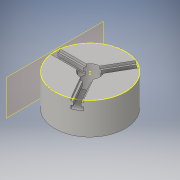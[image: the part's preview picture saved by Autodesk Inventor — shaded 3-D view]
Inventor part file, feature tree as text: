
AUTODESK INVENTOR PART (.ipt)
format: ipt  version: 2016 (Build 200138000, 138)  size: 259,584 bytes
history: native  units: in
note: dims shown in document units (in); Inventor stores cm internally (conversion verified against a paired STEP export)
features: sketch x13, extrude x11, plane x1, pattern_circular x1, projected_geometry x1
ambient origin geometry x8: Origin, YZ Plane, XZ Plane, XY Plane, X Axis, Y Axis, Z Axis, Center Point
bodies: Solid1 (feature_tree)
feature tree (27):
  extrude  "Extrusion1"  Depth=3.5787in
  extrude  "Extrusion2"  Depth=3.5787in
  sketch  "Sketch3"  dims[d13=1.1811in d15=360.0deg d17=0.2827in d18=0.0in]
  extrude  "Extrusion6"  Depth=0.2827in TaperAngle=0.0deg
  extrude  "Extrusion7"  Depth=0.3937in TaperAngle=0.0deg
  extrude  "Extrusion8"  Depth=0.3937in TaperAngle=0.0deg
  extrude  "Extrusion9"  Depth=0.3748in TaperAngle=0.0deg
  extrude  "Extrusion10"  Depth=0.3937in TaperAngle=0.0deg
  sketch  "Sketch12"  dims[d43=1.1811in d44=360.0deg d48=1.1811in d50=360.0deg]
  sketch  "Sketch13"  dims[d52=1.9685in d53=0.0in]
  plane  "Work Plane10"
  extrude  "Extrusion11"  Depth=1.1811in TaperAngle=360.0deg
  extrude  "Extrusion12"  [1 undecoded]
  extrude  "Extrusion13"  [1 undecoded]
  pattern_circular  "Circular Pattern1"  [2 undecoded]
  extrude  "Extrusion14"  [1 undecoded]
  sketch  "Sketch1"  dims[d1=3.5787in d2=0.0in d3=2.1701in]
  sketch  "Sketch2"  dims[d4=3.5787in d5=0.0in d6=0.5256in]
  sketch  "Sketch7"  dims[d19=0.3937in d20=0.0in d21=0.3937in d22=0.0in]
  sketch  "Sketch8"  dims[d23=0.3937in d24=0.0in d25=0.3937in d26=0.0in]
  sketch  "Sketch10"  dims[d36=0.3748in d37=2.9365in d38=0.0in]
  sketch  "Sketch11"  dims[d39=2.9365in d40=0.0in d41=0.3937in d42=0.0in]
  projected_geometry  "Projected Loop1"
  sketch  "Sketch16"
  sketch  "Sketch18"
  sketch  "Sketch20"
  sketch  "Sketch21"
note: 5 required parameter values undecoded (feature->parameter linkage not recoverable at this tier; creation-order binding heuristic only, values carry confidence <= 0.55)
